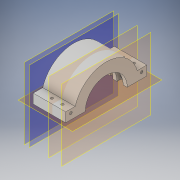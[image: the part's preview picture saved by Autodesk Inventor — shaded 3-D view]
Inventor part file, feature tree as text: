
AUTODESK INVENTOR PART (.ipt)
format: ipt  version: 2019 (Build 230136000, 136)  size: 534,016 bytes
history: native  units: mm
features: sketch x26, extrude x21, mirror x13, plane x12, projected_geometry x11, other x4, fillet x4, hole x3
ambient origin geometry x8: Origin, YZ Plane, XZ Plane, XY Plane, X Axis, Y Axis, Z Axis, Center Point
bodies: Body1 (feature_tree)
feature tree (94):
  other  "實體1"
  extrude  "擠出1"  Depth=123.43mm
  plane  "工作平面2"
  extrude  "擠出3"  Depth=160.0mm
  plane  "工作平面3"
  extrude  "擠出4"  Depth=120.0mm TaperAngle=0.0deg
  extrude  "擠出5"  [1 undecoded]
  plane  "工作平面4"
  extrude  "擠出7"  Depth=130.0mm
  plane  "工作平面5"
  extrude  "擠出9"  Depth=15.0mm TaperAngle=0.0deg
  extrude  "擠出10"  [1 undecoded]
  extrude  "擠出11"  Depth=111.375mm
  extrude  "擠出12"  Depth=10.0mm TaperAngle=0.0deg
  mirror  "鏡射1"
  fillet  "圓角2"  Radius=10.0mm
  fillet  "圓角3"  Radius=10.0mm
  sketch  "草圖16"
  plane  "工作平面7"
  mirror  "鏡射2"
  fillet  "圓角5"  [1 undecoded]
  fillet  "圓角6"  Radius=10.0mm
  plane  "工作平面8"
  plane  "工作平面9"
  sketch  "草圖20"
  extrude  "擠出15"  [1 undecoded]
  plane  "工作平面10"
  extrude  "擠出16"  Depth=10.0mm
  extrude  "擠出17"  Depth=10.0mm TaperAngle=0.0deg
  plane  "工作平面11"
  extrude  "擠出19"  Depth=10.0mm TaperAngle=0.0deg
  extrude  "擠出20"  Depth=160.0mm
  mirror  "鏡射3"
  mirror  "鏡射4"
  extrude  "擠出21"  Depth=80.0mm
  mirror  "鏡射7"
  plane  "工作平面15"
  mirror  "鏡射9"
  hole  "孔2"  [1 undecoded]
  mirror  "鏡射10"
  mirror  "鏡射11"
  hole  "孔3"  [1 undecoded]
  mirror  "鏡射12"
  mirror  "鏡射13"
  extrude  "擠出22"  Depth=160.0mm
  extrude  "擠出23"  Depth=120.0mm TaperAngle=0.0deg
  extrude  "擠出24"  Depth=120.0mm TaperAngle=0.0deg
  extrude  "擠出25"  Depth=25.0mm
  extrude  "擠出27"  Depth=20.0mm
  extrude  "擠出28"  Depth=2.0mm
  mirror  "鏡射14"
  plane  "工作平面17"
  hole  "孔4"  [1 undecoded]
  mirror  "鏡射15"
  mirror  "鏡射16"
  other  "分割2"
  other  "分割3"
  other  "分割4"
  sketch  "草圖1"
  sketch  "草圖4"
  sketch  "草圖6"
  sketch  "草圖7"
  projected_geometry  "投影迴路1"
  sketch  "草圖9"
  projected_geometry  "投影迴路4"
  sketch  "草圖11"
  sketch  "草圖12"
  projected_geometry  "投影迴路6"
  sketch  "草圖13"
  projected_geometry  "投影迴路7"
  sketch  "草圖14"
  plane  "工作平面6"
  sketch  "草圖17"
  projected_geometry  "投影迴路8"
  sketch  "草圖24"
  projected_geometry  "投影迴路11"
  sketch  "草圖25"
  sketch  "草圖26"
  sketch  "草圖27"
  sketch  "草圖28"
  sketch  "草圖29"
  projected_geometry  "投影迴路12"
  sketch  "草圖30"
  sketch  "草圖31"
  sketch  "草圖32"
  projected_geometry  "投影迴路13"
  projected_geometry  "投影迴路14"
  projected_geometry  "投影迴路15"
  sketch  "草圖33"
  sketch  "草圖34"
  sketch  "草圖35"
  projected_geometry  "投影迴路16"
  sketch  "草圖36"
  sketch  "草圖37"
note: 7 required parameter values undecoded (feature->parameter linkage not recoverable at this tier; creation-order binding heuristic only, values carry confidence <= 0.55)
